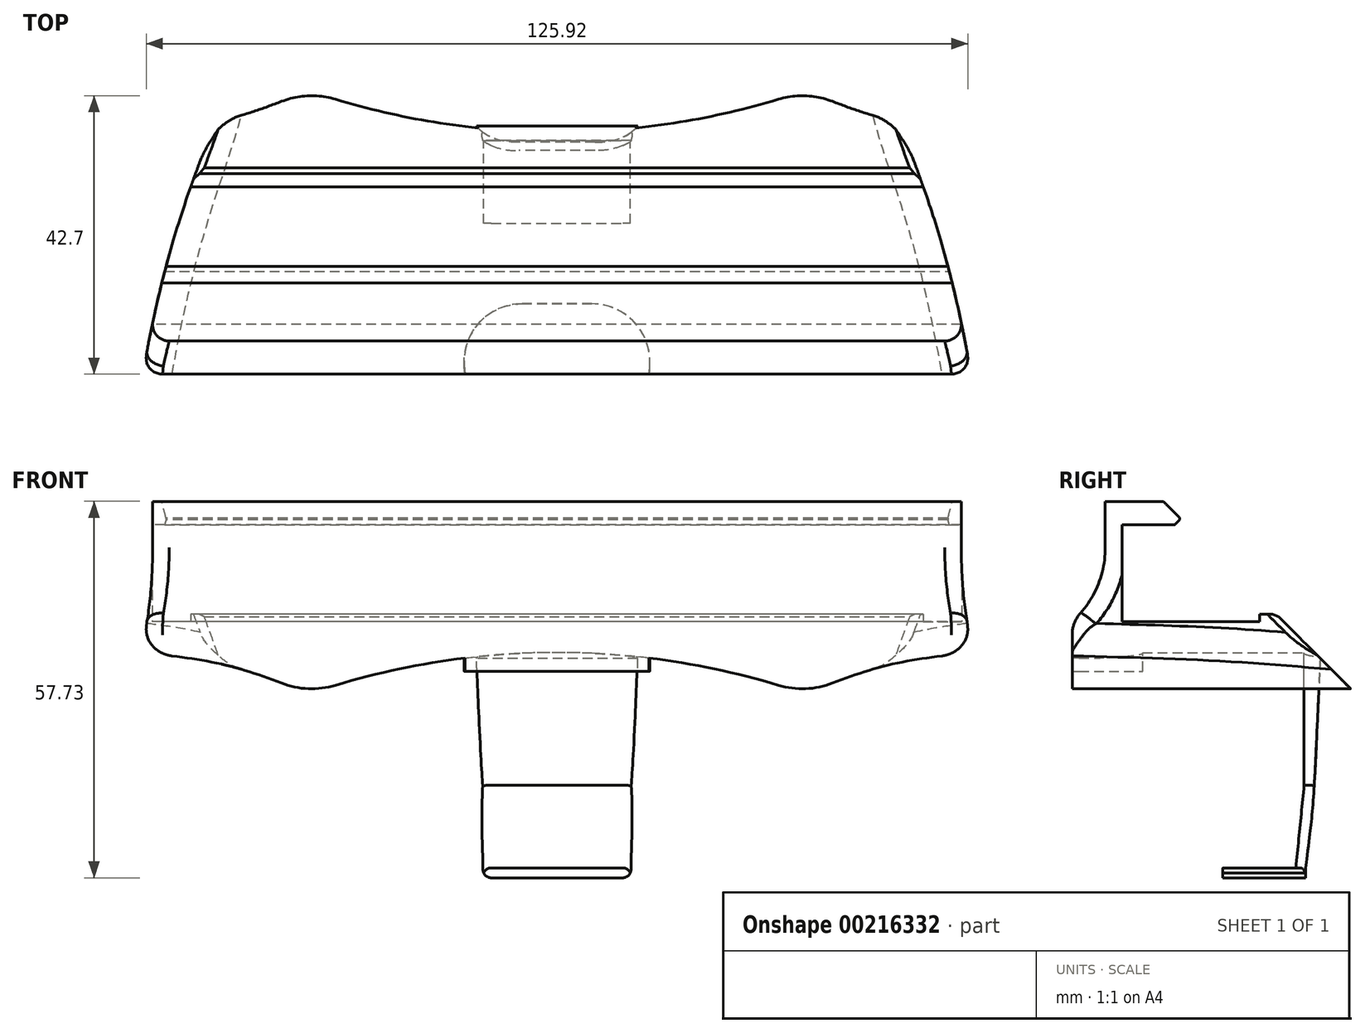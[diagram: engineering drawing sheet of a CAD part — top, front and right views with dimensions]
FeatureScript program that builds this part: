
annotation { "Feature Type Name" : "Feature", "Feature Type Description" : "" }
export const myFeature = defineFeature(function(context is Context, id is Id, definition is map)
    precondition{}
    {
        {
            var Q0;
            Q0=qCreatedBy(makeId("Front.planeOp"),FACE);
            var sketch = newSketch(context, id + "F0", { "sketchPlane" : qUnion([Q0])});
            skLineSegment(sketch, "E0", {"start": v(-44.8, 0) * mm, "end": v(-38.1, 0) * mm, "construction": true});
            skLineSegment(sketch, "E1", {"start": v(-38.1, 38.31) * mm, "end": v(-38.1, -29.68) * mm, "construction": true});
            skLineSegment(sketch, "E2", {"start": v(38.1, -24.74) * mm, "end": v(38.1, 33.54) * mm, "construction": true});
            skLineSegment(sketch, "E3", {"start": v(-57.58, -4.76) * mm, "end": v(65.6, -4.76) * mm, "construction": true});
            skLineSegment(sketch, "E4", {"start": v(-67.64, -11.11) * mm, "end": v(63.39, -11.11) * mm, "construction": true});
            skPoint(sketch, "E5.first.point", {"position": v(-38.1, 4.32) * mm});
            skPoint(sketch, "E5.second.point", {"position": v(0, 0) * mm});
            skPoint(sketch, "E5.third.point", {"position": v(38.1, 3.05) * mm});
            skArc(sketch, "E6", {"start": v(38.1, -11.11) * mm, "mid": v(19.31, -6.36) * mm, "end": v(0, -4.76) * mm});
            skPoint(sketch, "E6.first.point", {"position": v(-38.1, -11.11) * mm});
            skPoint(sketch, "E6.second.point", {"position": v(0, -4.76) * mm});
            skPoint(sketch, "E6.third.point", {"position": v(38.1, -11.11) * mm});
            skLineSegment(sketch, "E7", {"start": v(-38.1, 4.32) * mm, "end": v(-38.1, -11.11) * mm});
            skLineSegment(sketch, "E8", {"start": v(38.1, -11.11) * mm, "end": v(38.1, 3.05) * mm});
            skLineSegment(sketch, "E9", {"start": v(0, 0) * mm, "end": v(0, -4.76) * mm});
            skLineSegment(sketch, "E10.trimOffspring", {"start": v(0, 0) * mm, "end": v(44.36, 0) * mm, "construction": true});
            skLineSegment(sketch, "E11.trimOffspring", {"start": v(40.92, 3.05) * mm, "end": v(61.54, 3.05) * mm, "construction": true});
            skLineSegment(sketch, "E12", {"start": v(0, 0) * mm, "end": v(-2.13, 304.8) * mm, "construction": true});
            skPoint(sketch, "E12.endSnap0", {"position": v(-2.13, -11.11) * mm});
            skPoint(sketch, "E13", {"position": v(49.82, 3.05) * mm});
            skPoint(sketch, "E14.orphan", {"position": v(49.82, 25.92) * mm});
            skLineSegment(sketch, "E15", {"start": v(0, 0) * mm, "end": v(49.82, 0) * mm});
            skLineSegment(sketch, "E16", {"start": v(63.5, -4.76) * mm, "end": v(63.5, 0) * mm});
            skLineSegment(sketch, "E17", {"start": v(63.5, 0) * mm, "end": v(49.82, 0) * mm});
            skFitSpline(sketch, "E18", {"points": [v(38.1, -11.11) * mm, v(50.1, -6.86) * mm, v(63.5, -4.76) * mm], "startDerivative": vector(23.9, 9.76) * mm, "endDerivative": vector(26.89, 2.97) * mm});
            skSolve(sketch);
        }
        {
            var Q0;
            Q0=qCreatedBy(makeId("Top.planeOp"),FACE);
            var Q1;
            Q1=qBodyType(qCreatedBy(id+"Fd3kxMa9oh8c0KB_1",EDGE),BodyType.WIRE);
            cPlane(context, id + "F1", {"entities" : qUnion([Q0, Q1]), "cplaneType" : CPlaneType.OFFSET, "offset" : 2.54 * mm, "oppositeDirection" : true, "width" : 152.4 * mm, "height" : 152.4 * mm});
        }
        {
            var Q0;
            Q0=qSketchRegion(id+"F0",true);
            extrude(context, id + "F2", {"entities" : qUnion([Q0]), "depth" : 76.2 * mm});
        }
        {
            var Q0;
            Q0=makeQuery(id+"F2.opExtrude","SWEPT_FACE",FACE,{"disambiguationData":[OSD([sQuery(id+"F0.wireOp",EDGE,"E15"),sQuery(id+"F0.wireOp",EDGE,"E17")])]});
            var sketch = newSketch(context, id + "F3", { "sketchPlane" : qUnion([Q0])});
            skArc(sketch, "E19.0", {"start": v(43.16, 6.08) * mm, "mid": v(43.16, 6.2) * mm, "end": v(43.16, 6.3) * mm});
            skLineSegment(sketch, "E20.0", {"start": v(43.16, 6.08) * mm, "end": v(43.16, 6.3) * mm});
            skLineSegment(sketch, "E21", {"start": v(34, -9.35) * mm, "end": v(35.31, -8.43) * mm});
            skPoint(sketch, "E22.orphan", {"position": v(43.65, 25.65) * mm});
            skPoint(sketch, "E23.0.end.orphan", {"position": v(30.48, -16.11) * mm});
            skLineSegment(sketch, "E24", {"start": v(63.5, -76.2) * mm, "end": v(63.5, 0) * mm});
            skLineSegment(sketch, "E25", {"start": v(63.5, 0) * mm, "end": v(51.02, 0) * mm});
            skFitSpline(sketch, "E26", {"points": [v(51.02, 0) * mm, v(51.02, -31.37) * mm, v(63.5, -76.2) * mm], "startDerivative": vector(-3.82, -73) * mm, "endDerivative": vector(26.35, -149.47) * mm});
            skSolve(sketch);
        }
        {
            var Q0;
            Q0=qCreatedBy(id+"F1.planeOp",FACE);
            var sketch = newSketch(context, id + "F4", { "sketchPlane" : qUnion([Q0])});
            skLineSegment(sketch, "E27", {"start": v(0, -65.4) * mm, "end": v(15.11, -65.4) * mm});
            skLineSegment(sketch, "E28", {"start": v(0, -76.2) * mm, "end": v(14.1, -76.2) * mm});
            skLineSegment(sketch, "E29", {"start": v(14.1, -76.2) * mm, "end": v(15.11, -65.4) * mm});
            skPoint(sketch, "E30.visualSharp", {"position": v(15.11, -65.4) * mm});
            skPoint(sketch, "E31.end.orphan", {"position": v(0, -76.2) * mm});
            skPoint(sketch, "E31.start.orphan", {"position": v(0, -65.4) * mm});
            skLineSegment(sketch, "E32", {"start": v(0, -76.2) * mm, "end": v(0, -65.4) * mm});
            skSolve(sketch);
        }
        {
            var Q0;
            Q0=qSketchRegion(id+"F4",true);
            extrude(context, id + "F5", {"entities" : qUnion([Q0]), "operationType" : NewBodyOperationType.ADD, "oppositeDirection" : true, "depth" : 5.08 * mm});
        }
        {
            var Q0;
            Q0=makeQuery(id+"F5.opExtrude","SWEPT_EDGE",EDGE,{"disambiguationData":[OSD([sQuery(id+"F4.wireOp",EDGE,"E27"),sQuery(id+"F4.wireOp",EDGE,"E29")])]});
            fillet(context, id + "F6", {"entities" : qUnion([Q0]), "radius" : 8.9 * mm, "tangentPropagation" : true, "allowEdgeOverflow" : false});
        }
        {
            var Q0;
            Q0=makeQuery(id+"F12.boolean.opBoolean","MERGE",FACE,{"derivedFrom":[makeQuery(id+"F5.boolean.opBoolean","MERGE",FACE,{"derivedFrom":[makeQuery(id+"FKUtFNTr2oPPhhn_1.boolean.opBoolean","MERGE",FACE,{"derivedFrom":[makeQuery(id+"F2.opExtrude","SWEPT_FACE",FACE,{"disambiguationData":[OSD([sQuery(id+"F0.wireOp",EDGE,"E9")])]}),makeQuery(id+"FKUtFNTr2oPPhhn_1.opExtrude","SWEPT_FACE",FACE,{"disambiguationData":[OSD([sQuery(id+"Fd3kxMa9oh8c0KB_1.wireOp",EDGE,"JlagjkWO-SAIo-8z09-lU7S-WVjPN6ih7MiH")])]})]}),makeQuery(id+"F5.opExtrude","SWEPT_FACE",FACE,{"disambiguationData":[OSD([sQuery(id+"F4.wireOp",EDGE,"E32")])]})]}),makeQuery(id+"F12.opExtrude","SWEPT_FACE",FACE,{"disambiguationData":[OSD([sQuery(id+"F11.wireOp",EDGE,"E41")])]})]});
            var sketch = newSketch(context, id + "F7", { "sketchPlane" : qUnion([Q0])});
            skLineSegment(sketch, "E33", {"start": v(40.39, -37.78) * mm, "end": v(41.91, -37.78) * mm});
            skLineSegment(sketch, "E34", {"start": v(41.91, -37.78) * mm, "end": v(40.64, -25.08) * mm});
            skLineSegment(sketch, "E35", {"start": v(40.64, -25.08) * mm, "end": v(40.64, -4.76) * mm});
            skLineSegment(sketch, "E36", {"start": v(40.64, -4.76) * mm, "end": v(38.1, -4.76) * mm});
            skFitSpline(sketch, "E37", {"points": [v(40.39, -37.78) * mm, v(39.4, -29.24) * mm, v(38.1, -4.76) * mm], "startDerivative": vector(-2.03, 19.88) * mm, "endDerivative": vector(-2.75, 51.05) * mm});
            skLineSegment(sketch, "E38", {"start": v(38.1, -4.76) * mm, "end": v(38.1, -35.95) * mm, "construction": true});
            skSolve(sketch);
        }
        {
            var Q0;
            Q0=qSketchRegion(id+"F7",true);
            extrude(context, id + "F8", {"entities" : qUnion([Q0]), "operationType" : NewBodyOperationType.ADD, "oppositeDirection" : true, "depth" : 13.97 * mm});
        }
        {
            var Q0;
            Q0=makeQuery(id+"F8.opExtrude","SWEPT_EDGE",EDGE,{"disambiguationData":[OSD([sQuery(id+"F7.wireOp",EDGE,"E33"),sQuery(id+"F7.wireOp",EDGE,"E37")])]});
            var Q1;
            Q1=qCreatedBy(makeId("Front.planeOp"),FACE);
            cPlane(context, id + "F9", {"entities" : qUnion([Q0, Q1]), "cplaneType" : CPlaneType.LINE_ANGLE, "offset" : 25.4 * mm, "angle" : 0 * degree, "width" : 152.4 * mm, "height" : 152.4 * mm});
        }
        {
            var Q0;
            Q0=makeQuery(id+"F8.opExtrude","CAP_EDGE",EDGE,{"disambiguationData":[OSD([sQuery(id+"F7.wireOp",EDGE,"E34")])],"isStart":false});
            var Q1;
            Q1=makeQuery(id+"F8.opExtrude","CAP_EDGE",EDGE,{"disambiguationData":[OSD([sQuery(id+"F7.wireOp",EDGE,"E35")])],"isStart":false});
            fillet(context, id + "F10", {"entities" : qUnion([Q0, Q1]), "radius" : 8.13 * mm, "tangentPropagation" : true, "rho" : 0.5, "crossSection" : FilletCrossSection.CONIC, "allowEdgeOverflow" : false});
        }
        {
            var Q0;
            Q0=qCreatedBy(id+"F9.planeOp",FACE);
            var sketch = newSketch(context, id + "F11", { "sketchPlane" : qUnion([Q0])});
            skLineSegment(sketch, "E39", {"start": v(0, -37.78) * mm, "end": v(-11.35, -37.78) * mm});
            skLineSegment(sketch, "E40", {"start": v(-11.35, -37.78) * mm, "end": v(-11.35, -39.3) * mm});
            skLineSegment(sketch, "E41", {"start": v(0, -37.78) * mm, "end": v(0, -39.3) * mm});
            skLineSegment(sketch, "E42", {"start": v(0, -39.3) * mm, "end": v(-11.35, -39.3) * mm});
            skSolve(sketch);
        }
        {
            var Q0;
            Q0=qSketchRegion(id+"F11",true);
            extrude(context, id + "F12", {"entities" : qUnion([Q0]), "operationType" : NewBodyOperationType.ADD, "oppositeDirection" : true, "depth" : 12.7 * mm});
        }
        {
            var Q0;
            Q0=makeQuery(id+"F12.opExtrude","SWEPT_EDGE",EDGE,{"disambiguationData":[OSD([sQuery(id+"F11.wireOp",EDGE,"E40"),sQuery(id+"F11.wireOp",EDGE,"353efbc5-a89a-4849-a3c2-711c67ee4f1c")])]});
            fillet(context, id + "F13", {"entities" : qUnion([Q0]), "radius" : 1.27 * mm, "tangentPropagation" : true, "allowEdgeOverflow" : false});
        }
        {
            var Q0;
            Q0=qCreatedBy(makeId("Right.planeOp"),FACE);
            var sketch = newSketch(context, id + "F14", { "sketchPlane" : qUnion([Q0])});
            skLineSegment(sketch, "E43", {"start": v(-71.12, 0) * mm, "end": v(-71.12, 18.42) * mm});
            skLineSegment(sketch, "E44", {"start": v(-71.12, 18.41) * mm, "end": v(-62.23, 18.41) * mm});
            skLineSegment(sketch, "E45", {"start": v(-62.23, 18.42) * mm, "end": v(-62.23, 14.86) * mm});
            skLineSegment(sketch, "E46", {"start": v(-62.23, 14.86) * mm, "end": v(-68.58, 14.86) * mm});
            skLineSegment(sketch, "E47", {"start": v(-68.58, 14.86) * mm, "end": v(-68.58, 0) * mm});
            skLineSegment(sketch, "E48", {"start": v(-68.58, 0) * mm, "end": v(-71.12, 0) * mm});
            skSolve(sketch);
        }
        {
            var Q0;
            Q0=qSketchRegion(id+"F14",true);
            extrude(context, id + "F15", {"entities" : qUnion([Q0]), "operationType" : NewBodyOperationType.ADD, "depth" : 63.5 * mm});
        }
        {
            var Q0;
            Q0=qCreatedBy(makeId("Right.planeOp"),FACE);
            var sketch = newSketch(context, id + "F16", { "sketchPlane" : qUnion([Q0])});
            skLineSegment(sketch, "E49", {"start": v(-77.75, 33.93) * mm, "end": v(32.59, -76.4) * mm});
            skLineSegment(sketch, "E50", {"start": v(34.65, -78.46) * mm, "end": v(34.65, 33.93) * mm});
            skLineSegment(sketch, "E51", {"start": v(-77.75, 33.93) * mm, "end": v(34.65, 33.93) * mm});
            skLineSegment(sketch, "E52", {"start": v(-24.2, -19.61) * mm, "end": v(-24.2, -19.61) * mm});
            skLineSegment(sketch, "E53", {"start": v(-24.2, -19.61) * mm, "end": v(34.65, -78.46) * mm});
            skSolve(sketch);
        }
        {
            var Q0;
            Q0=makeQuery(id+"F15.opExtrude","SWEPT_FACE",FACE,{"disambiguationData":[OSD([sQuery(id+"F14.wireOp",EDGE,"E45")])]});
            var sketch = newSketch(context, id + "F17", { "sketchPlane" : qUnion([Q0])});
            skLineSegment(sketch, "E54", {"start": v(-63.5, 18.42) * mm, "end": v(-63.5, 14.86) * mm});
            skLineSegment(sketch, "E55", {"start": v(-63.5, 14.86) * mm, "end": v(0, 14.86) * mm});
            skLineSegment(sketch, "E56", {"start": v(0, 14.86) * mm, "end": v(0, 18.42) * mm});
            skLineSegment(sketch, "E57", {"start": v(0, 18.42) * mm, "end": v(-63.5, 18.42) * mm});
            skSolve(sketch);
        }
        {
            var Q0;
            Q0=qSketchRegion(id+"F17",true);
            extrude(context, id + "F18", {"entities" : qUnion([Q0]), "operationType" : NewBodyOperationType.ADD, "depth" : 2.54 * mm});
        }
        {
            var Q0;
            Q0=qSketchRegion(id+"F16",true);
            extrude(context, id + "F19", {"entities" : qUnion([Q0]), "operationType" : NewBodyOperationType.REMOVE, "endBound" : BoundingType.THROUGH_ALL, "oppositeDirection" : true, "depth" : 25.4 * mm, "hasSecondDirection" : true, "secondDirectionBound" : SecondDirectionBoundingType.THROUGH_ALL, "secondDirectionOppositeDirection" : false, "secondDirectionDepth" : 25.4 * mm});
        }
        {
            var Q0;
            Q0=makeQuery(id+"F18.boolean.opBoolean","MERGE",FACE,{"derivedFrom":[makeQuery(id+"F15.boolean.opBoolean","MERGE",FACE,{"derivedFrom":[makeQuery(id+"F12.boolean.opBoolean","MERGE",FACE,{"derivedFrom":[makeQuery(id+"F8.boolean.opBoolean","MERGE",FACE,{"derivedFrom":[makeQuery(id+"F5.boolean.opBoolean","MERGE",FACE,{"derivedFrom":[makeQuery(id+"F2.opExtrude","SWEPT_FACE",FACE,{"disambiguationData":[OSD([sQuery(id+"F0.wireOp",EDGE,"E9")])]}),makeQuery(id+"F5.opExtrude","SWEPT_FACE",FACE,{"disambiguationData":[OSD([sQuery(id+"F4.wireOp",EDGE,"E32")])]})]}),makeQuery(id+"F8.opExtrude","CAP_FACE",FACE,{"disambiguationData":[OSD([sQuery(id+"F7.wireOp",EDGE,"lnBXM0yI-dSRE-VfLJ-7HZ5-BXpm3VU3eFl9"),sQuery(id+"F7.wireOp",EDGE,"E33"),sQuery(id+"F7.wireOp",EDGE,"E34"),sQuery(id+"F7.wireOp",EDGE,"E35"),sQuery(id+"F7.wireOp",EDGE,"E36")])],"isStart":true})]}),makeQuery(id+"F12.opExtrude","SWEPT_FACE",FACE,{"disambiguationData":[OSD([sQuery(id+"F11.wireOp",EDGE,"E41")])]})]}),makeQuery(id+"F15.opExtrude","CAP_FACE",FACE,{"disambiguationData":[OSD([sQuery(id+"F14.wireOp",EDGE,"E43"),sQuery(id+"F14.wireOp",EDGE,"E44"),sQuery(id+"F14.wireOp",EDGE,"E45"),sQuery(id+"F14.wireOp",EDGE,"E46"),sQuery(id+"F14.wireOp",EDGE,"E47"),sQuery(id+"F14.wireOp",EDGE,"E48")])],"isStart":true})]}),makeQuery(id+"F18.opExtrude","SWEPT_FACE",FACE,{"disambiguationData":[OSD([sQuery(id+"F17.wireOp",EDGE,"E56")])]})]});
            var sketch = newSketch(context, id + "F20", { "sketchPlane" : qUnion([Q0])});
            skLineSegment(sketch, "E58", {"start": v(43.82, 0) * mm, "end": v(44.9, 1.1) * mm});
            skLineSegment(sketch, "E59", {"start": v(44.9, 1.1) * mm, "end": v(47.45, 1.1) * mm});
            skLineSegment(sketch, "E60", {"start": v(47.45, 1.1) * mm, "end": v(47.45, 0) * mm});
            skLineSegment(sketch, "E61", {"start": v(47.45, 0) * mm, "end": v(43.82, 0) * mm});
            skSolve(sketch);
        }
        {
            var Q0;
            Q0=qSketchRegion(id+"F20",true);
            var Q1;
            Q1=makeQuery(id+"F18.boolean.opBoolean","MERGE",FACE,{"derivedFrom":[makeQuery(id+"F15.boolean.opBoolean","MERGE",FACE,{"derivedFrom":[makeQuery(id+"F2.opExtrude","SWEPT_FACE",FACE,{"disambiguationData":[OSD([sQuery(id+"F0.wireOp",EDGE,"E16")])]}),makeQuery(id+"F15.opExtrude","CAP_FACE",FACE,{"disambiguationData":[OSD([sQuery(id+"F14.wireOp",EDGE,"E43"),sQuery(id+"F14.wireOp",EDGE,"E44"),sQuery(id+"F14.wireOp",EDGE,"E45"),sQuery(id+"F14.wireOp",EDGE,"E46"),sQuery(id+"F14.wireOp",EDGE,"E47"),sQuery(id+"F14.wireOp",EDGE,"E48")])],"isStart":false})]}),makeQuery(id+"F18.opExtrude","SWEPT_FACE",FACE,{"disambiguationData":[OSD([sQuery(id+"F17.wireOp",EDGE,"E54")])]})]});
            extrude(context, id + "F21", {"entities" : qUnion([Q0]), "operationType" : NewBodyOperationType.ADD, "endBound" : BoundingType.UP_TO_SURFACE, "oppositeDirection" : true, "endBoundEntityFace" : qUnion([Q1]), "depth" : 25.4 * mm});
        }
        {
            var Q0;
            Q0=qSketchRegion(id+"F3",true);
            extrude(context, id + "F22", {"entities" : qUnion([Q0]), "operationType" : NewBodyOperationType.REMOVE, "depth" : 25.4 * mm, "hasSecondDirection" : true, "secondDirectionOppositeDirection" : true, "secondDirectionDepth" : 25.4 * mm});
        }
        {
            var Q0;
            Q0=makeQuery(id+"F15.opExtrude","SWEPT_EDGE",EDGE,{"disambiguationData":[OSD([sQuery(id+"F14.wireOp",EDGE,"E43"),sQuery(id+"F14.wireOp",EDGE,"E48")])]});
            fillet(context, id + "F23", {"entities" : qUnion([Q0]), "radius" : 15.24 * mm, "tangentPropagation" : true, "allowEdgeOverflow" : false});
        }
        {
            var Q0;
            Q0=makeQuery(id+"F23.opFillet","BLEND_EDGE",EDGE,{"blendedFrom":[makeQuery(id+"F15.opExtrude","SWEPT_EDGE",EDGE,{"disambiguationData":[OSD([sQuery(id+"F14.wireOp",EDGE,"E43"),sQuery(id+"F14.wireOp",EDGE,"E48")])]}),makeQuery(id+"F5.boolean.opBoolean","MERGE",FACE,{"derivedFrom":[makeQuery(id+"F2.opExtrude","CAP_FACE",FACE,{"disambiguationData":[OSD([sQuery(id+"F0.wireOp",EDGE,"E6"),sQuery(id+"F0.wireOp",EDGE,"E9"),sQuery(id+"F0.wireOp",EDGE,"E15"),sQuery(id+"F0.wireOp",EDGE,"E16"),sQuery(id+"F0.wireOp",EDGE,"E17"),sQuery(id+"F0.wireOp",EDGE,"UeOzVpdf-vl8X-Ht22-uxWY-bhk5w6YBKlPA")])],"isStart":false}),makeQuery(id+"F5.opExtrude","SWEPT_FACE",FACE,{"disambiguationData":[OSD([sQuery(id+"F4.wireOp",EDGE,"E28")])]})]})],"blendedInto":[makeQuery(id+"F5.boolean.opBoolean","MERGE",FACE,{"derivedFrom":[makeQuery(id+"F2.opExtrude","CAP_FACE",FACE,{"disambiguationData":[OSD([sQuery(id+"F0.wireOp",EDGE,"E6"),sQuery(id+"F0.wireOp",EDGE,"E9"),sQuery(id+"F0.wireOp",EDGE,"E15"),sQuery(id+"F0.wireOp",EDGE,"E16"),sQuery(id+"F0.wireOp",EDGE,"E17"),sQuery(id+"F0.wireOp",EDGE,"UeOzVpdf-vl8X-Ht22-uxWY-bhk5w6YBKlPA")])],"isStart":false}),makeQuery(id+"F5.opExtrude","SWEPT_FACE",FACE,{"disambiguationData":[OSD([sQuery(id+"F4.wireOp",EDGE,"E28")])]})]})]});
            fillet(context, id + "F24", {"entities" : qUnion([Q0]), "radius" : 5.08 * mm, "tangentPropagation" : true, "allowEdgeOverflow" : false});
        }
        {
            var Q0;
            Q0=makeQuery(id+"F2.opExtrude","SWEPT_BODY",BODY,{"disambiguationData":[OSD([sQuery(id+"F0.wireOp",EDGE,"E6"),sQuery(id+"F0.wireOp",EDGE,"SAt3LVdG-wE4P-Vml7-PRrg-NZ9h65sIcNej"),sQuery(id+"F0.wireOp",EDGE,"E9"),sQuery(id+"F0.wireOp",EDGE,"00606892-b09f-41bf-b1d9-afd14dc3a5f1.trimOffspring")])]});
            var Q1;
            Q1=makeQuery(id+"FvmywHwUOoOG8US_1.opExtrude","SWEPT_BODY",BODY,{"disambiguationData":[OSD([sQuery(id+"F4.wireOp",EDGE,"E27"),sQuery(id+"F4.wireOp",EDGE,"E31"),sQuery(id+"F4.wireOp",EDGE,"E28"),sQuery(id+"F4.wireOp",EDGE,"E29")])]});
            var Q2;
            Q2=qCreatedBy(makeId("Right.planeOp"),FACE);
            mirror(context, id + "F25", {"operationType" : NewBodyOperationType.ADD, "entities" : qUnion([Q0, Q1]), "mirrorPlane" : qUnion([Q2])});
        }
        {
            var Q0;
            Q0=qCreatedBy(makeId("Right.planeOp"),FACE);
            var sketch = newSketch(context, id + "F26", { "sketchPlane" : qUnion([Q0])});
            skLineSegment(sketch, "E62", {"start": v(-117.4, -15.14) * mm, "end": v(-56.96, 45.3) * mm, "construction": true});
            skLineSegment(sketch, "E63", {"start": v(-117.4, -15.14) * mm, "end": v(-6.97, -15.14) * mm, "construction": true});
            skSolve(sketch);
        }
        {
            var Q0;
            Q0=makeQuery(id+"F25.opPattern","COPY",EDGE,{"derivedFrom":makeQuery(id+"F22.boolean.opBoolean","MERGE",EDGE,{"derivedFrom":[makeQuery(id+"F2.opExtrude","CAP_EDGE",EDGE,{"disambiguationData":[OSD([sQuery(id+"F0.wireOp",EDGE,"E16")])],"isStart":false}),makeQuery(id+"F22.opExtrude","SWEPT_EDGE",EDGE,{"disambiguationData":[OSD([sQuery(id+"F0.wireOp",EDGE,"E15"),sQuery(id+"F0.wireOp",EDGE,"E17"),sQuery(id+"F3.wireOp",EDGE,"E24"),sQuery(id+"F3.wireOp",EDGE,"E26")])]})]}),"instanceName":"1"});
            fillet(context, id + "F27", {"entities" : qUnion([Q0]), "radius" : 2.54 * mm, "tangentPropagation" : true, "allowEdgeOverflow" : false});
        }
        {
            var Q0;
            Q0=makeQuery(id+"F22.boolean.opBoolean","MERGE",EDGE,{"derivedFrom":[makeQuery(id+"F2.opExtrude","CAP_EDGE",EDGE,{"disambiguationData":[OSD([sQuery(id+"F0.wireOp",EDGE,"E16")])],"isStart":false}),makeQuery(id+"F22.opExtrude","SWEPT_EDGE",EDGE,{"disambiguationData":[OSD([sQuery(id+"F0.wireOp",EDGE,"E15"),sQuery(id+"F0.wireOp",EDGE,"E17"),sQuery(id+"F3.wireOp",EDGE,"E24"),sQuery(id+"F3.wireOp",EDGE,"E26")])]})]});
            fillet(context, id + "F28", {"entities" : qUnion([Q0]), "radius" : 2.54 * mm, "tangentPropagation" : true, "allowEdgeOverflow" : false});
        }
        {
            var Q0;
            Q0=makeQuery(id+"F25.opPattern","COPY",EDGE,{"derivedFrom":makeQuery(id+"F22.boolean.opBoolean","INTERSECT",EDGE,{"derivedFrom":[makeQuery(id+"F21.boolean.opBoolean","MERGE",FACE,{"derivedFrom":[makeQuery(id+"F19.boolean.opBoolean","COPY",FACE,{"disambiguationData":[TD([makeQuery(id+"F2.opExtrude","SWEPT_FACE",FACE,{"disambiguationData":[OSD([sQuery(id+"F0.wireOp",EDGE,"E6")])]})])],"derivedFrom":makeQuery(id+"F19.opExtrude","SWEPT_FACE",FACE,{"disambiguationData":[OSD([sQuery(id+"F16.wireOp",EDGE,"E49"),sQuery(id+"F16.wireOp",EDGE,"E53")])]})}),makeQuery(id+"F21.opExtrude","SWEPT_FACE",FACE,{"disambiguationData":[OSD([sQuery(id+"F20.wireOp",EDGE,"E58")])]})]}),makeQuery(id+"F22.opExtrude","SWEPT_FACE",FACE,{"disambiguationData":[OSD([sQuery(id+"F3.wireOp",EDGE,"E26")])]})]}),"instanceName":"1"});
            var Q1;
            Q1=makeQuery(id+"F22.boolean.opBoolean","INTERSECT",EDGE,{"derivedFrom":[makeQuery(id+"F21.boolean.opBoolean","MERGE",FACE,{"derivedFrom":[makeQuery(id+"F19.boolean.opBoolean","COPY",FACE,{"disambiguationData":[TD([makeQuery(id+"F2.opExtrude","SWEPT_FACE",FACE,{"disambiguationData":[OSD([sQuery(id+"F0.wireOp",EDGE,"E6")])]})])],"derivedFrom":makeQuery(id+"F19.opExtrude","SWEPT_FACE",FACE,{"disambiguationData":[OSD([sQuery(id+"F16.wireOp",EDGE,"E49"),sQuery(id+"F16.wireOp",EDGE,"E53")])]})}),makeQuery(id+"F21.opExtrude","SWEPT_FACE",FACE,{"disambiguationData":[OSD([sQuery(id+"F20.wireOp",EDGE,"E58")])]})]}),makeQuery(id+"F22.opExtrude","SWEPT_FACE",FACE,{"disambiguationData":[OSD([sQuery(id+"F3.wireOp",EDGE,"E26")])]})]});
            var Q2;
            {var subQ0=makeQuery(id+"F21.opExtrude","SWEPT_EDGE",EDGE,{"disambiguationData":[OSD([sQuery(id+"F20.wireOp",EDGE,"E58"),sQuery(id+"F20.wireOp",EDGE,"E59")])]});Q2=makeQuery(id+"F25.boolean.opBoolean","MERGE",EDGE,{"derivedFrom":[subQ0,makeQuery(id+"F25.opPattern","COPY",EDGE,{"derivedFrom":subQ0,"instanceName":"1"})]});}
            chamfer(context, id + "F29", {"entities" : qUnion([Q0, Q1, Q2]), "width" : 1.27 * mm, "tangentPropagation" : true});
        }
        {
            var Q0;
            Q0=makeQuery(id+"F2.opExtrude","SWEPT_EDGE",EDGE,{"disambiguationData":[OSD([sQuery(id+"F0.wireOp",EDGE,"E6"),sQuery(id+"F0.wireOp",EDGE,"E8"),sQuery(id+"F0.wireOp",EDGE,"E18")])]});
            var Q1;
            Q1=makeQuery(id+"F25.opPattern","COPY",EDGE,{"derivedFrom":makeQuery(id+"F2.opExtrude","SWEPT_EDGE",EDGE,{"disambiguationData":[OSD([sQuery(id+"F0.wireOp",EDGE,"E6"),sQuery(id+"F0.wireOp",EDGE,"E8"),sQuery(id+"F0.wireOp",EDGE,"E18")])]}),"instanceName":"1"});
            fillet(context, id + "F30", {"entities" : qUnion([Q0, Q1]), "radius" : 12.7 * mm, "tangentPropagation" : true, "allowEdgeOverflow" : false});
        }
        {
            var Q0;
            Q0=makeQuery(id+"F22.boolean.opBoolean","INTERSECT",EDGE,{"derivedFrom":[makeQuery(id+"F2.opExtrude","SWEPT_FACE",FACE,{"disambiguationData":[OSD([sQuery(id+"F0.wireOp",EDGE,"E18")])]}),makeQuery(id+"F22.opExtrude","SWEPT_FACE",FACE,{"disambiguationData":[OSD([sQuery(id+"F3.wireOp",EDGE,"E26")])]})]});
            var Q1;
            Q1=makeQuery(id+"F25.opPattern","COPY",EDGE,{"derivedFrom":makeQuery(id+"F22.boolean.opBoolean","INTERSECT",EDGE,{"derivedFrom":[makeQuery(id+"F2.opExtrude","SWEPT_FACE",FACE,{"disambiguationData":[OSD([sQuery(id+"F0.wireOp",EDGE,"E18")])]}),makeQuery(id+"F22.opExtrude","SWEPT_FACE",FACE,{"disambiguationData":[OSD([sQuery(id+"F3.wireOp",EDGE,"E26")])]})]}),"instanceName":"1"});
            fillet(context, id + "F31", {"entities" : qUnion([Q0, Q1]), "radius" : 5.08 * mm, "allowEdgeOverflow" : false});
        }
        {
            var Q0;
            {var subQ0=makeQuery(id+"F18.opExtrude","CAP_EDGE",EDGE,{"disambiguationData":[OSD([sQuery(id+"F17.wireOp",EDGE,"E55")])],"isStart":false});Q0=makeQuery(id+"F25.boolean.opBoolean","MERGE",EDGE,{"derivedFrom":[subQ0,makeQuery(id+"F25.opPattern","COPY",EDGE,{"derivedFrom":subQ0,"instanceName":"1"})]});}
            chamfer(context, id + "F32", {"entities" : qUnion([Q0]), "width" : 0.76 * mm, "tangentPropagation" : true});
        }
    });
